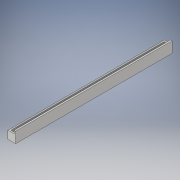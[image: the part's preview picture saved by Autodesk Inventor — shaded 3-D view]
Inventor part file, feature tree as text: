
AUTODESK INVENTOR PART (.ipt)
format: ipt  version: 2019.4 (Build 234330000, 330)  size: 121,856 bytes
history: native  units: mm
features: extrude x3, sketch x3, other x1
ambient origin geometry x8: Origin, YZ Plane, XZ Plane, XY Plane, X Axis, Y Axis, Z Axis, Center Point
bodies: Body1 (feature_tree)
feature tree (7):
  other  "Sólido1"
  extrude  "Extrusão1"  Depth=10.0mm
  extrude  "Extrusão2"  Depth=50.0mm
  extrude  "Extrusão3"  Depth=70.0mm
  sketch  "Esboço1"  dims[d0=10.0mm d1=10.0mm]
  sketch  "Esboço2"  dims[d2=10.0mm d3=50.0mm]
  sketch  "Esboço3"  dims[d4=50.0mm d5=70.0mm d6=1010.0mm d7=0.0mm d8=10.0mm d9=0.0mm d10=10.0mm d11=0.0mm]
